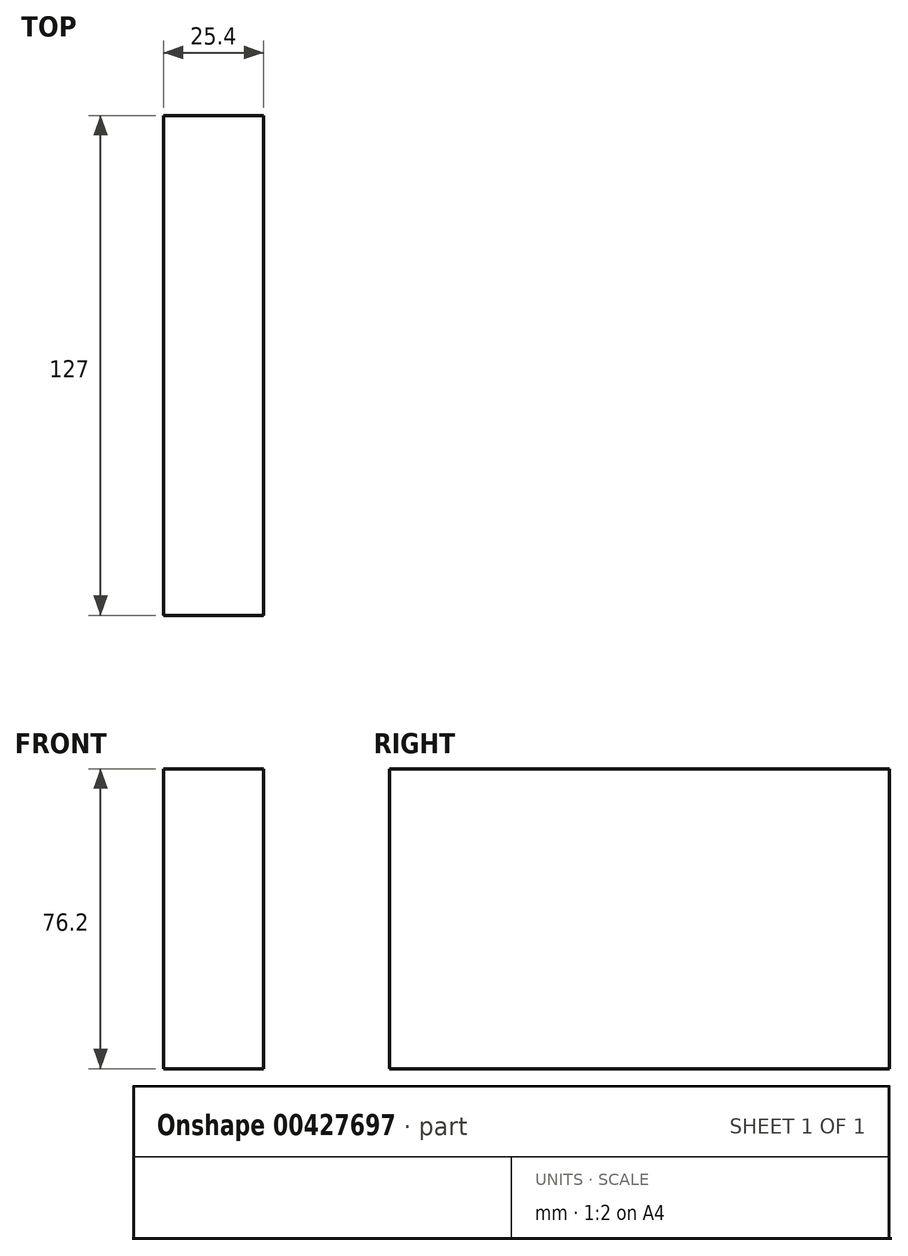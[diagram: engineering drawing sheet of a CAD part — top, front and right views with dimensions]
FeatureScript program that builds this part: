
annotation { "Feature Type Name" : "Feature", "Feature Type Description" : "" }
export const myFeature = defineFeature(function(context is Context, id is Id, definition is map)
    precondition{}
    {
        {
            var Q0;
            Q0=qCreatedBy(makeId("Right.planeOp"),FACE);
            var sketch = newSketch(context, id + "F0", { "sketchPlane" : qUnion([Q0])});
            skLineSegment(sketch, "E0.bottom", {"start": v(63.5, -38.1) * mm, "end": v(-63.5, -38.1) * mm});
            skLineSegment(sketch, "E0.top", {"start": v(63.5, 38.1) * mm, "end": v(-63.5, 38.1) * mm});
            skLineSegment(sketch, "E0.left", {"start": v(63.5, -38.1) * mm, "end": v(63.5, 38.1) * mm});
            skLineSegment(sketch, "E0.right", {"start": v(-63.5, -38.1) * mm, "end": v(-63.5, 38.1) * mm});
            skPoint(sketch, "E0.middle", {"position": v(0, 0) * mm});
            skSolve(sketch);
        }
        {
            var Q0;
            Q0=qSketchRegion(id+"F0",true);
            extrude(context, id + "F1", {"entities" : qUnion([Q0]), "depth" : 25.4 * mm});
        }
    });
